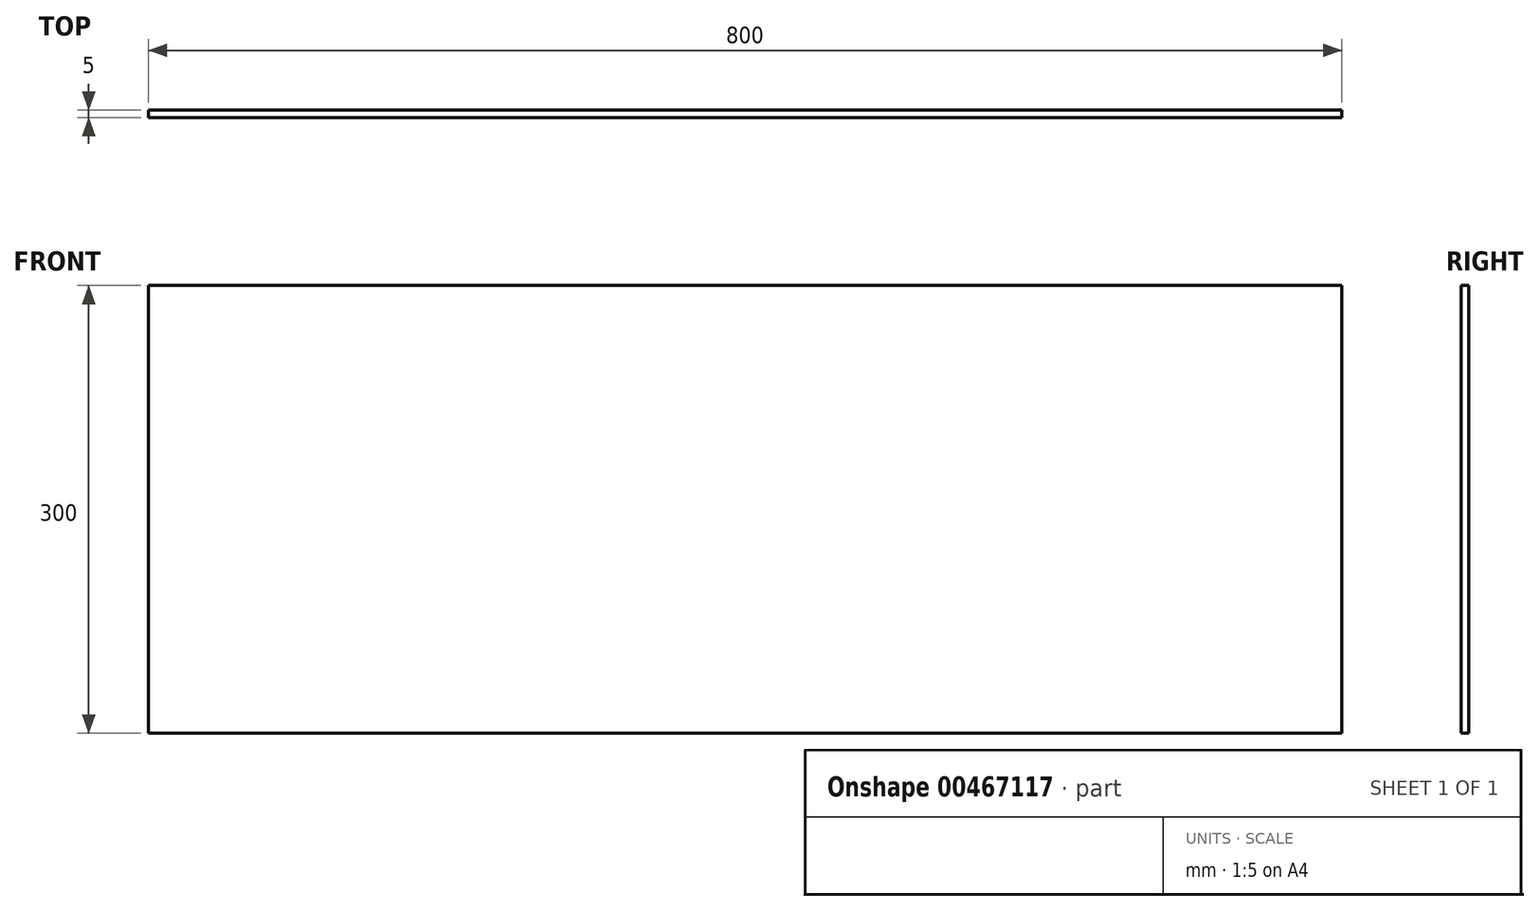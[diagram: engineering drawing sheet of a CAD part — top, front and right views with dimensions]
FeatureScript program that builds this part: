
annotation { "Feature Type Name" : "Feature", "Feature Type Description" : "" }
export const myFeature = defineFeature(function(context is Context, id is Id, definition is map)
    precondition{}
    {
        {
            var Q0;
            Q0=qCreatedBy(makeId("Front.planeOp"),FACE);
            var sketch = newSketch(context, id + "F0", { "sketchPlane" : qUnion([Q0])});
            skLineSegment(sketch, "E0.bottom", {"start": v(-298.9, 300) * mm, "end": v(501.1, 300) * mm});
            skLineSegment(sketch, "E0.top", {"start": v(-298.9, 0) * mm, "end": v(501.1, 0) * mm});
            skLineSegment(sketch, "E0.left", {"start": v(-298.9, 300) * mm, "end": v(-298.9, 0) * mm});
            skLineSegment(sketch, "E0.right", {"start": v(501.1, 300) * mm, "end": v(501.1, 0) * mm});
            skSolve(sketch);
        }
        {
            var Q0;
            Q0=makeQuery(id+"F0.imprint","IMPRINT",FACE,{"disambiguationData":[TD([[makeQuery(id+"F0.imprint","IMPRINT",EDGE,{"derivedFrom":sQuery(id+"F0.wireOp",EDGE,"E0.bottom")}),-1.0]])]});
            extrude(context, id + "F1", {"entities" : qUnion([Q0]), "depth" : 5 * mm});
        }
    });
